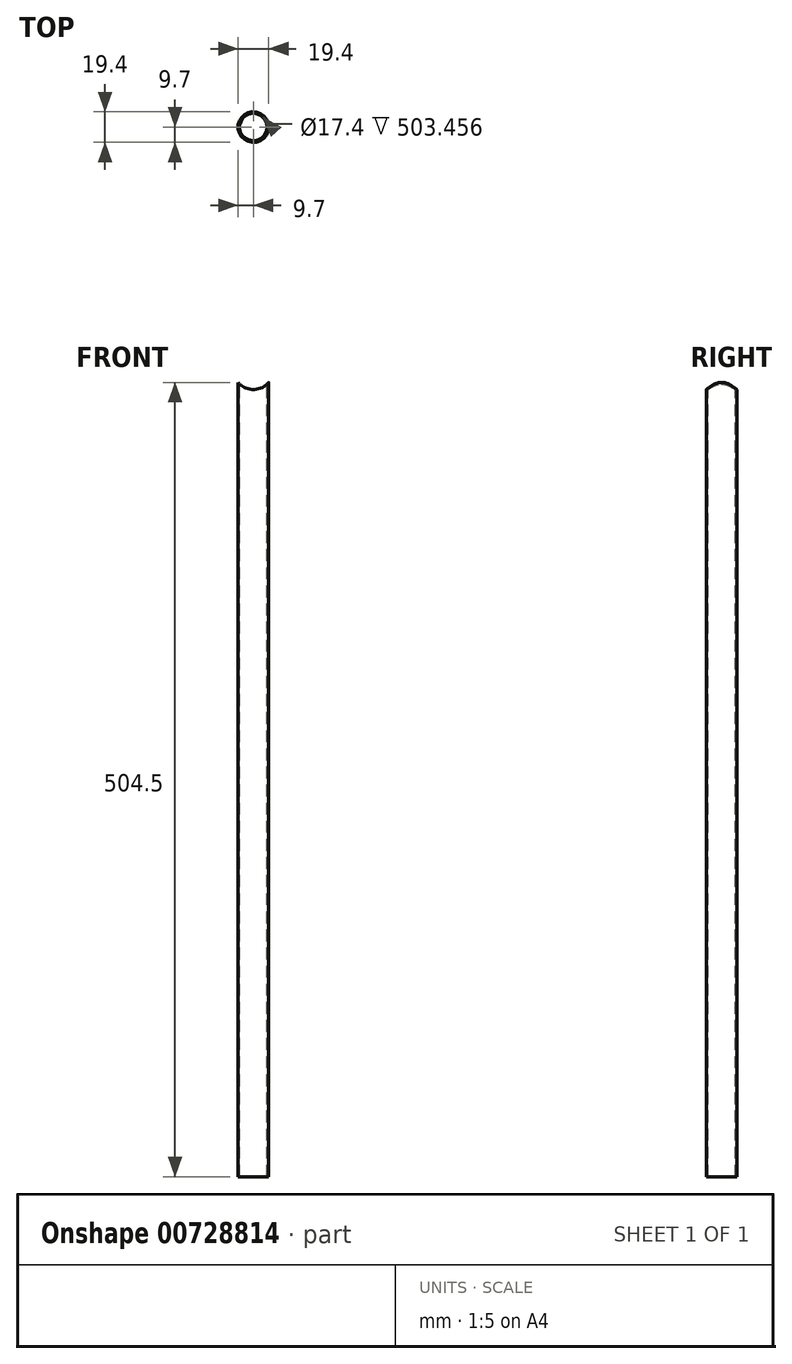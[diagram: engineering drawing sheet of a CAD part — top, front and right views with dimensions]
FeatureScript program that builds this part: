
annotation { "Feature Type Name" : "Feature", "Feature Type Description" : "" }
export const myFeature = defineFeature(function(context is Context, id is Id, definition is map)
    precondition{}
    {
        {
            var Q0;
            Q0=qCreatedBy(makeId("Top.planeOp"),FACE);
            var sketch = newSketch(context, id + "F0", { "sketchPlane" : qUnion([Q0])});
            skCircle(sketch, "E0", {"center": v(0, 0) * mm, "radius": 9.7 * mm});
            skCircle(sketch, "E1", {"center": v(0, 0) * mm, "radius": 8.7 * mm});
            skSolve(sketch);
        }
        {
            var Q0;
            Q0 = qSketchRegion(id + "F0", true);
            extrude(context, id + "F1", {"entities" : qUnion([Q0]), "oppositeDirection" : true, "depth" : 500 * mm, "offsetDistance" : 25 * mm});
        }
        {
            var Q0;
            Q0=qCreatedBy(makeId("Front.planeOp"),FACE);
            var sketch = newSketch(context, id + "F2", { "sketchPlane" : qUnion([Q0])});
            skArc(sketch, "E2", {"start": v(-9.7, 4.5) * mm, "mid": v(0, 0) * mm, "end": v(9.7, 4.5) * mm});
            skLineSegment(sketch, "E3", {"start": v(9.7, 4.5) * mm, "end": v(9.7, 10) * mm});
            skLineSegment(sketch, "E4", {"start": v(-9.7, 4.5) * mm, "end": v(-9.7, 10) * mm});
            skLineSegment(sketch, "E5", {"start": v(-9.7, 10) * mm, "end": v(9.7, 10) * mm});
            skPoint(sketch, "E6.start.orphan", {"position": v(0, 0) * mm});
            skSolve(sketch);
        }
        {
            var Q0;
            Q0 = qSketchRegion(id + "F0", true);
            extrude(context, id + "F3", {"entities" : qUnion([Q0]), "operationType" : NewBodyOperationType.ADD, "depth" : 10 * mm, "offsetDistance" : 25 * mm});
        }
        {
            var Q0;
            Q0 = qSketchRegion(id + "F2", true);
            extrude(context, id + "F4", {"entities" : qUnion([Q0]), "operationType" : NewBodyOperationType.REMOVE, "endBound" : BoundingType.SYMMETRIC, "oppositeDirection" : true, "depth" : 25 * mm, "offsetDistance" : 25 * mm});
        }
    });
